# Revit family: FU_Chair_Sandler_Charme 2-1
name_source: partatom
category: Furniture
units: mm (PartAtom-declared; Revit-internal decimal feet)

## family parameters
Always vertical = Yes
Cut with Voids When Loaded = No
OmniClass Number = 23.40.20.00
OmniClass Title = General Furniture and Specialties
Room Calculation Point = No
Shared = No
Work Plane-Based = No

## types (1)
- Charme 2.1
    Arm Width = 565 mm  [stored 1.85367 ft]
    Default Elevation = 0 mm  [stored 0 ft]
    Depth = 555 mm  [stored 1.82087 ft]
    Description = Upholstered armchair, beechwood frame and wooden accent on back.
    Frame = Wood - Beech - Desert Aniline
    Height = 870 mm  [stored 2.85433 ft]
    Manufacturer = Sandler
    Model = Charme 2.1
    Seat = Fabric - Gravity - Frost CPC32
    URL = https://www.sandlerseating.com
    Width = 490 mm  [stored 1.60761 ft]

note: [stored X ft] marks values corroborated as IEEE doubles in the binary element streams (Revit-internal decimal feet)

## geometry (parser evidence)
native form markers: Sweep x4
no freeform markers — native parametric forms only
